# Revit family: Interlocked switched 200_250V
name_source: partatom
category: Installations électriques
revit_build: Autodesk Revit 2018 (Build: 20170223_1515(x64)
units: mm (PartAtom-declared; Revit-internal decimal feet)

## family parameters
Conserver l'orientation des annotations = Non
Cote de connecteur circulaire = Utiliser le diamètre
Couper avec des vides une fois chargée = Non
Hôte = Face
Partagée = Non
Point de calcul de pièce = Non
Type d'élément = Normal

## types (2) — shared parameters
Elévation par défaut = 1000 mm  [stored 3.28084 ft]
Fabricant = Legrand
International standard socket for flush mounting or surface mounting with accessory allows the connection of power devices = International standard socket for flush mounting or surface mounting with accessory allows the connection of power devices
Maximum use temperature = +40
Minimum use temperature = -25
Number of poles = 3
Position of earth h = 6
Product family = 0852-P17
Standard IEC or NFC = IEC
Tension V = 230 V  50/60 Hz blue
characteristic color = blue
connecting type = screw terminals
depth for flush mounting mm = 81 mm  [stored 0.265748 ft]
depth mm = 120 mm  [stored 0.393701 ft]
halogen free = Oui
height mm = 105 mm  [stored 0.344488 ft]
horizontal fixing distance mm = 91 mm
intensity A = 16 A
interlocking type = electrical and mechanical locking
material of box = plastic
vertical fixing distance mm = 87 mm
width mm = 125 mm  [stored 0.410105 ft]

## per-type parameters (varying)
| type | Description | Modèle | protection class IP | resistance to chocks IK |
| P17 - IP44 - 200/250V - 16A -2P+E | LG-057320_Interlocked switched socket with small flange P17 - IP55 - 200/250V - 16A -2P+E | LG-057320 | IP55 | 11 |
| P17 - IP55 - 200/250V - 16A -2P+E | LG-057300_Interlocked switched socket with small flange P17 - IP44 - 200/250V - 16A -2P+E | LG-057300 | IP44 | 08 |

note: [stored X ft] marks values corroborated as IEEE doubles in the binary element streams (Revit-internal decimal feet)
